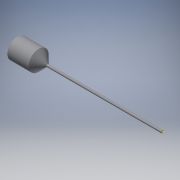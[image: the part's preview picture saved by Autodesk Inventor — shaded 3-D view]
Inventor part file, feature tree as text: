
AUTODESK INVENTOR PART (.ipt)
format: ipt  version: 2018 (Build 220112000, 112)  size: 103,936 bytes
history: native  units: in
note: dims shown in document units (in); Inventor stores cm internally (conversion verified against a paired STEP export)
features: revolve x1, other x1, sketch x1
ambient origin geometry x8: Origin, YZ Plane, XZ Plane, XY Plane, X Axis, Y Axis, Z Axis, Center Point
bodies: Solid1 (feature_tree)
feature tree (3):
  revolve  "Revolution1"  [1 undecoded]
  other  "Work Point1"
  sketch  "Sketch1"  dims[d0=0.125in d1=11.5in d2=1.0in d3=3.0in d4=90.0deg d5=45.0deg]
note: 1 required parameter value undecoded (feature->parameter linkage not recoverable at this tier; creation-order binding heuristic only, values carry confidence <= 0.55)
